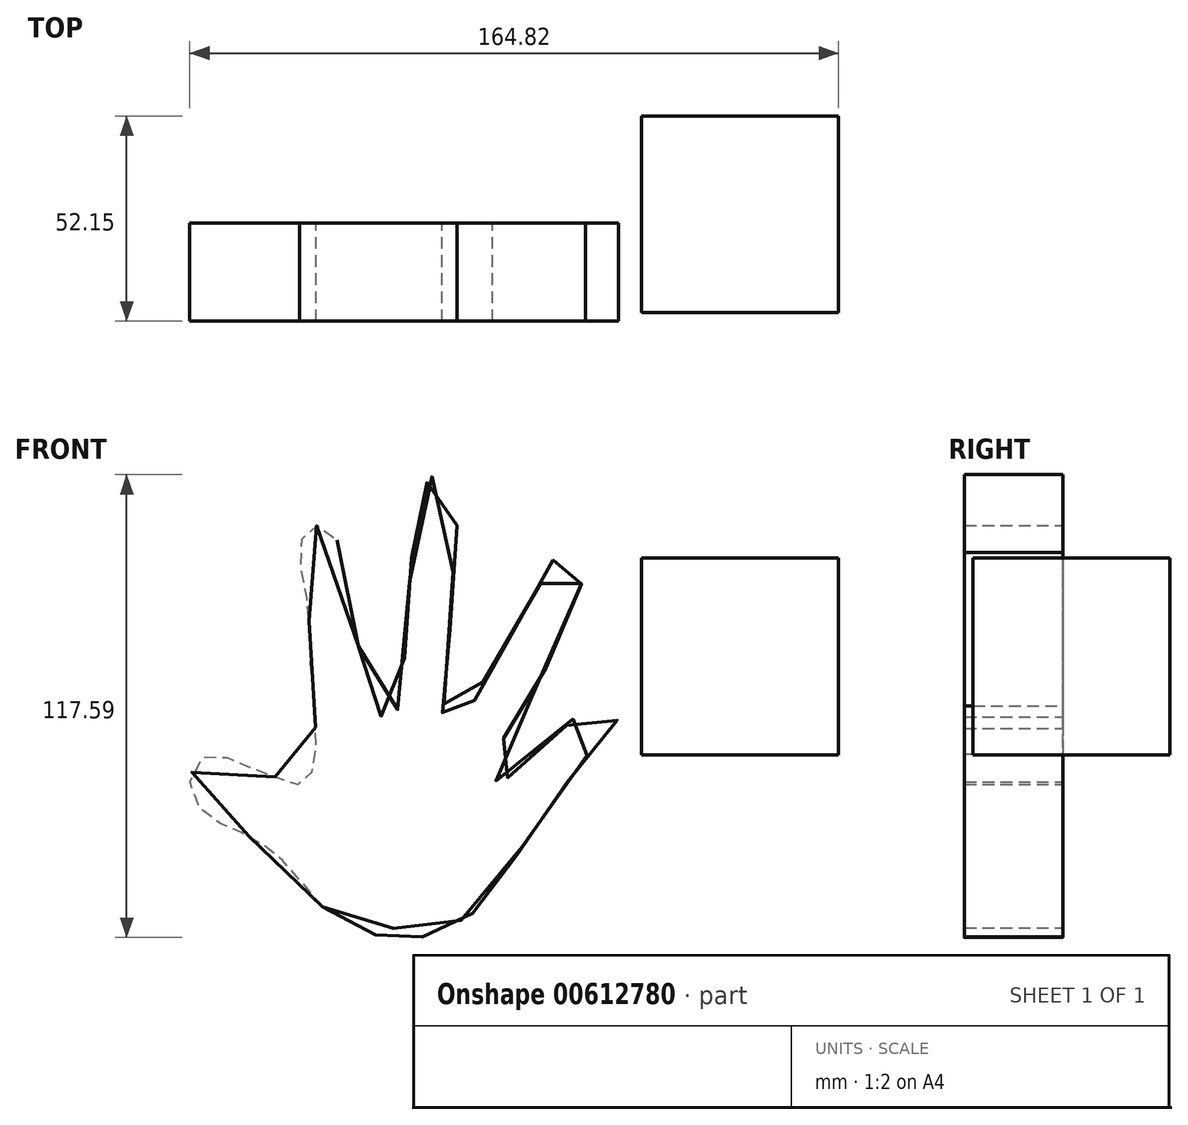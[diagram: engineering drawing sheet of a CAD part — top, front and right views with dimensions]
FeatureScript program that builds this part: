
annotation { "Feature Type Name" : "Feature", "Feature Type Description" : "" }
export const myFeature = defineFeature(function(context is Context, id is Id, definition is map)
    precondition{}
    {
        {
            var Q0;
            Q0=qCreatedBy(makeId("Top.planeOp"),FACE);
            var sketch = newSketch(context, id + "F0", { "sketchPlane" : qUnion([Q0])});
            skLineSegment(sketch, "E0.bottom", {"start": v(-26.27, 27.15) * mm, "end": v(23.73, 27.15) * mm});
            skLineSegment(sketch, "E0.top", {"start": v(-26.27, -22.85) * mm, "end": v(23.73, -22.85) * mm});
            skLineSegment(sketch, "E0.left", {"start": v(-26.27, 27.15) * mm, "end": v(-26.27, -22.85) * mm});
            skLineSegment(sketch, "E0.right", {"start": v(23.73, 27.15) * mm, "end": v(23.73, -22.85) * mm});
            skSolve(sketch);
        }
        {
            var Q0;
            Q0 = qSketchRegion(id + "F0", true);
            extrude(context, id + "F1", {"entities" : qUnion([Q0]), "depth" : 50 * mm, "offsetDistance" : 25 * mm});
        }
        {
            var Q0;
            Q0=qCreatedBy(makeId("Front.planeOp"),FACE);
            var sketch = newSketch(context, id + "F2", { "sketchPlane" : qUnion([Q0])});
            skFitSpline(sketch, "E1", {"points": [v(-107.28, -38.58) * mm, v(-116.02, -28.39) * mm, v(-121.55, -23.44) * mm, v(-129.41, -19.07) * mm, v(-135.52, -16.16) * mm, v(-141.06, -8.3) * mm, v(-136.69, 0) * mm, v(-128.25, -2.18) * mm, v(-120.39, -5.1) * mm, v(-113.4, -7.42) * mm, v(-109.9, -4.22) * mm, v(-109.03, 5.39) * mm, v(-109.61, 15.28) * mm, v(-110.49, 25.47) * mm, v(-111.36, 40.03) * mm, v(-113.1, 52.26) * mm, v(-109.9, 58.08) * mm, v(-104.08, 55.17) * mm, v(-99.42, 34.8) * mm, v(-95.93, 16.16) * mm, v(-93.6, 10.34) * mm, v(-89.23, 10.34) * mm, v(-86.9, 18.78) * mm, v(-85.74, 37.12) * mm, v(-84.58, 53.71) * mm, v(-83.41, 63.03) * mm, v(-78.46, 71.18) * mm, v(-73.8, 64.49) * mm, v(-73.8, 51.39) * mm, v(-74.97, 28.97) * mm, v(-75.84, 15.28) * mm, v(-76.71, 8.3) * mm, v(-73.22, 6.84) * mm, v(-68.56, 14.12) * mm, v(-63.03, 25.18) * mm, v(-55.46, 36.83) * mm, v(-50.51, 46.44) * mm, v(-46.15, 51.39) * mm, v(-40.9, 48.77) * mm, v(-42.36, 41.78) * mm, v(-48.47, 26.93) * mm, v(-54.59, 14.12) * mm, v(-61.28, 4.22) * mm, v(-64.2, -3.06) * mm, v(-62.74, -6.84) * mm, v(-54, 0) * mm, v(-46.73, 6.26) * mm, v(-38.87, 12.08) * mm, v(-32.17, 10.63) * mm, v(-40.03, 0) * mm, v(-44.98, -6.55) * mm, v(-54, -19.36) * mm, v(-60.12, -28.97) * mm, v(-66.52, -38.28) * mm, v(-71.77, -41.78) * mm, v(-75.84, -44.69) * mm, v(-82.25, -46.15) * mm, v(-86.61, -44.1) * mm, v(-90.4, -44.4) * mm, v(-95.06, -46.15) * mm, v(-99.13, -45.85) * mm, v(-107.28, -38.58) * mm]});
            skSolve(sketch);
        }
        {
            var Q0;
            Q0 = qSketchRegion(id + "F2", true);
            extrude(context, id + "F3", {"entities" : qUnion([Q0]), "depth" : 25 * mm, "offsetDistance" : 25 * mm});
        }
    });
